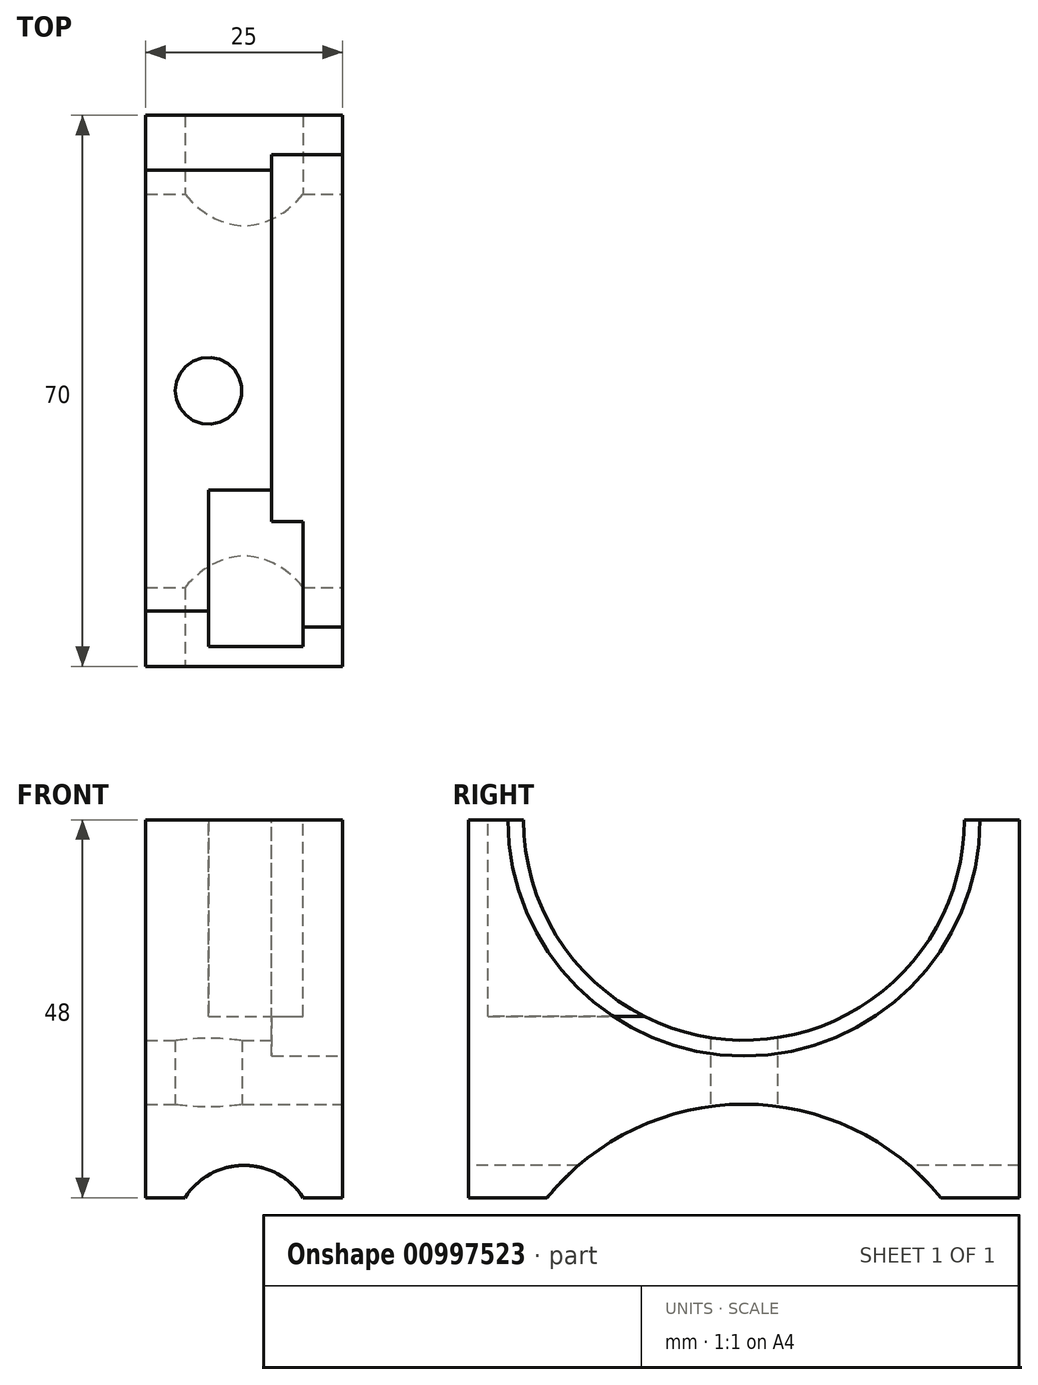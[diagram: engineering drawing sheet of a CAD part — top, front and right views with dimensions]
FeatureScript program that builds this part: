
annotation { "Feature Type Name" : "Feature", "Feature Type Description" : "" }
export const myFeature = defineFeature(function(context is Context, id is Id, definition is map)
    precondition{}
    {
        {
            var Q0;
            Q0=qCreatedBy(makeId("Right.planeOp"),FACE);
            var sketch = newSketch(context, id + "F0", { "sketchPlane" : qUnion([Q0])});
            skLineSegment(sketch, "E0.bottom", {"start": v(-35, 24) * mm, "end": v(35, 24) * mm});
            skLineSegment(sketch, "E0.top", {"start": v(-35, -24) * mm, "end": v(35, -24) * mm});
            skLineSegment(sketch, "E0.left", {"start": v(-35, 24) * mm, "end": v(-35, -24) * mm});
            skLineSegment(sketch, "E0.right", {"start": v(35, 24) * mm, "end": v(35, -24) * mm});
            skSolve(sketch);
        }
        {
            var Q0;
            Q0 = qSketchRegion(id + "F0", true);
            extrude(context, id + "F1", {"entities" : qUnion([Q0]), "depth" : 25 * mm, "offsetDistance" : 25 * mm});
        }
        {
            var Q0;
            Q0=makeQuery(id+"F1.opExtrude","CAP_FACE",FACE,{"disambiguationData":[OSD([sQuery(id+"F0.wireOp",EDGE,"E0.bottom"),sQuery(id+"F0.wireOp",EDGE,"E0.top"),sQuery(id+"F0.wireOp",EDGE,"E0.left"),sQuery(id+"F0.wireOp",EDGE,"E0.right")])],"isStart":false});
            var sketch = newSketch(context, id + "F2", { "sketchPlane" : qUnion([Q0])});
            skCircle(sketch, "E1", {"center": v(0, 24) * mm, "radius": 30 * mm});
            skSolve(sketch);
        }
        {
            var Q0;
            Q0 = qSketchRegion(id + "F2", true);
            extrude(context, id + "F3", {"entities" : qUnion([Q0]), "operationType" : NewBodyOperationType.REMOVE, "oppositeDirection" : true, "depth" : 9 * mm, "offsetDistance" : 25 * mm});
        }
        {
            var Q0;
            Q0=makeQuery(id+"F3.boolean.opBoolean","COPY",FACE,{"derivedFrom":makeQuery(id+"F3.opExtrude","CAP_FACE",FACE,{"disambiguationData":[OSD([sQuery(id+"F2.wireOp",EDGE,"E1")])],"isStart":false})});
            var sketch = newSketch(context, id + "F4", { "sketchPlane" : qUnion([Q0])});
            skCircle(sketch, "E2", {"center": v(0, 24) * mm, "radius": 28 * mm});
            skSolve(sketch);
        }
        {
            var Q0;
            Q0 = qSketchRegion(id + "F4", true);
            extrude(context, id + "F5", {"entities" : qUnion([Q0]), "operationType" : NewBodyOperationType.REMOVE, "oppositeDirection" : true, "depth" : 25 * mm, "offsetDistance" : 25 * mm});
        }
        {
            var Q0;
            Q0=makeQuery(id+"F1.opExtrude","SWEPT_FACE",FACE,{"disambiguationData":[OSD([sQuery(id+"F0.wireOp",EDGE,"E0.top")])]});
            var sketch = newSketch(context, id + "F6", { "sketchPlane" : qUnion([Q0])});
            skCircle(sketch, "E3", {"center": v(8, 0) * mm, "radius": 4.25 * mm});
            skPoint(sketch, "E3.centerSnap0", {"position": v(0, 0) * mm});
            skSolve(sketch);
        }
        {
            var Q0;
            Q0 = qSketchRegion(id + "F6", true);
            extrude(context, id + "F7", {"entities" : qUnion([Q0]), "operationType" : NewBodyOperationType.REMOVE, "oppositeDirection" : true, "depth" : 25 * mm, "offsetDistance" : 25 * mm});
        }
        {
            var Q0;
            {var subQ1=sQuery(id+"F0.wireOp",EDGE,"E0.left");var subQ4=sQuery(id+"F0.wireOp",EDGE,"E0.bottom");Q0=makeQuery(id+"F5.boolean.opBoolean","SPLIT",FACE,{"disambiguationData":[TD([makeQuery(id+"F1.opExtrude","SWEPT_FACE",FACE,{"disambiguationData":[OSD([subQ1])]})])],"derivedFrom":makeQuery(id+"F1.opExtrude","SWEPT_FACE",FACE,{"disambiguationData":[OSD([subQ4])]})});}
            var sketch = newSketch(context, id + "F8", { "sketchPlane" : qUnion([Q0])});
            skLineSegment(sketch, "E4.top", {"start": v(8, -32.5) * mm, "end": v(20, -32.5) * mm});
            skLineSegment(sketch, "E4.left", {"start": v(8, -28) * mm, "end": v(8, -32.5) * mm});
            skLineSegment(sketch, "E4.right", {"start": v(20, -27.5) * mm, "end": v(20, -32.5) * mm});
            skLineSegment(sketch, "E5", {"start": v(14, -24.06) * mm, "end": v(14, -38.59) * mm, "construction": true});
            skLineSegment(sketch, "E6.top", {"start": v(8, -10) * mm, "end": v(20, -10) * mm});
            skLineSegment(sketch, "E6.left", {"start": v(8, -28) * mm, "end": v(8, -10) * mm});
            skLineSegment(sketch, "E6.right", {"start": v(20, -27.5) * mm, "end": v(20, -10) * mm});
            skCircle(sketch, "E7.0", {"center": v(8, 0) * mm, "radius": 4.25 * mm, "construction": true});
            skSolve(sketch);
        }
        {
            var Q0;
            Q0 = qSketchRegion(id + "F8", true);
            extrude(context, id + "F9", {"entities" : qUnion([Q0]), "operationType" : NewBodyOperationType.REMOVE, "oppositeDirection" : true, "depth" : 25 * mm, "offsetDistance" : 25 * mm});
        }
        {
            var Q0;
            Q0=makeQuery(id+"F1.opExtrude","CAP_FACE",FACE,{"disambiguationData":[OSD([sQuery(id+"F0.wireOp",EDGE,"E0.bottom"),sQuery(id+"F0.wireOp",EDGE,"E0.top"),sQuery(id+"F0.wireOp",EDGE,"E0.left"),sQuery(id+"F0.wireOp",EDGE,"E0.right")])],"isStart":false});
            var sketch = newSketch(context, id + "F10", { "sketchPlane" : qUnion([Q0])});
            skArc(sketch, "E8", {"start": v(25, -24) * mm, "mid": v(0, -12.13) * mm, "end": v(-25, -24) * mm});
            skLineSegment(sketch, "E9", {"start": v(-25, -24) * mm, "end": v(-25, -30.53) * mm});
            skLineSegment(sketch, "E10", {"start": v(-25, -30.53) * mm, "end": v(25, -30.53) * mm});
            skLineSegment(sketch, "E11", {"start": v(25, -30.53) * mm, "end": v(25, -24) * mm});
            skSolve(sketch);
        }
        {
            var Q0;
            Q0 = qSketchRegion(id + "F10", true);
            extrude(context, id + "F11", {"entities" : qUnion([Q0]), "operationType" : NewBodyOperationType.REMOVE, "oppositeDirection" : true, "depth" : 25 * mm, "offsetDistance" : 25 * mm});
        }
        {
            var Q0;
            Q0=makeQuery(id+"F1.opExtrude","SWEPT_FACE",FACE,{"disambiguationData":[OSD([sQuery(id+"F0.wireOp",EDGE,"E0.left")])]});
            var sketch = newSketch(context, id + "F12", { "sketchPlane" : qUnion([Q0])});
            skArc(sketch, "E12", {"start": v(20, -24) * mm, "mid": v(12.5, -19.9) * mm, "end": v(5, -24) * mm});
            skLineSegment(sketch, "E13", {"start": v(5, -24) * mm, "end": v(5, -27.68) * mm});
            skLineSegment(sketch, "E14", {"start": v(5, -27.68) * mm, "end": v(20, -27.68) * mm});
            skLineSegment(sketch, "E15", {"start": v(20, -27.68) * mm, "end": v(20, -24) * mm});
            skSolve(sketch);
        }
        {
            var Q0;
            Q0 = qSketchRegion(id + "F12", true);
            extrude(context, id + "F13", {"entities" : qUnion([Q0]), "operationType" : NewBodyOperationType.REMOVE, "oppositeDirection" : true, "depth" : 75 * mm, "offsetDistance" : 25 * mm});
        }
    });
